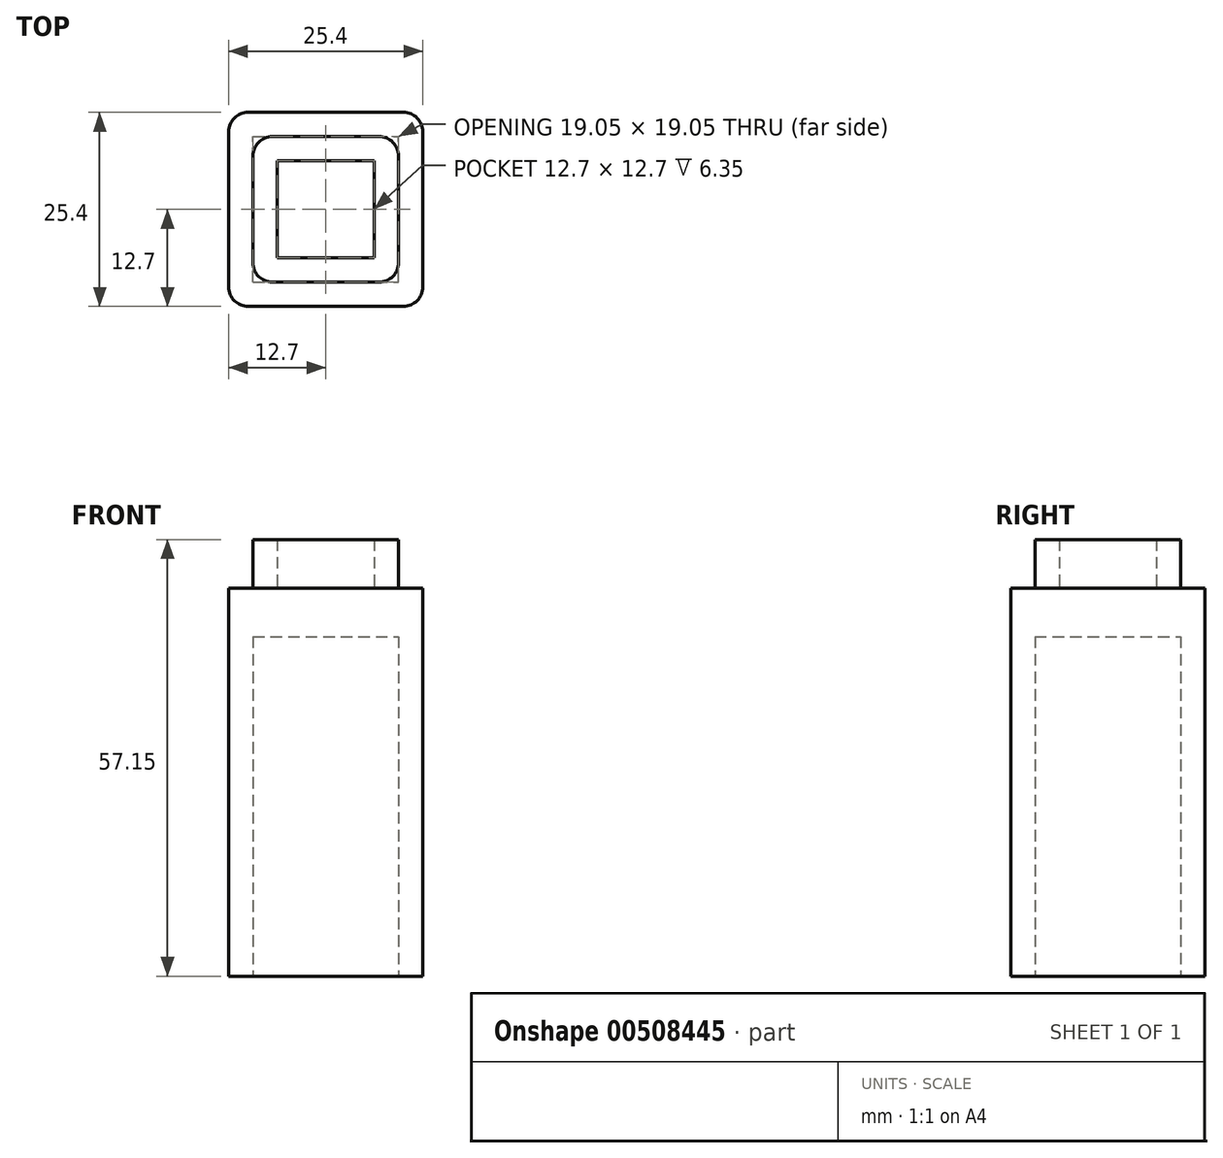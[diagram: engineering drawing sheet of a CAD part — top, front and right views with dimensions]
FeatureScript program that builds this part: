
annotation { "Feature Type Name" : "Feature", "Feature Type Description" : "" }
export const myFeature = defineFeature(function(context is Context, id is Id, definition is map)
    precondition{}
    {
        {
            var Q0;
            Q0=qCreatedBy(makeId("Top.planeOp"),FACE);
            var sketch = newSketch(context, id + "F0", { "sketchPlane" : qUnion([Q0])});
            skLineSegment(sketch, "E0.bottom", {"start": v(0, 0) * mm, "end": v(25.4, 0) * mm});
            skLineSegment(sketch, "E0.top", {"start": v(0, -25.4) * mm, "end": v(25.4, -25.4) * mm});
            skLineSegment(sketch, "E0.left", {"start": v(0, 0) * mm, "end": v(0, -25.4) * mm});
            skLineSegment(sketch, "E0.right", {"start": v(25.4, 0) * mm, "end": v(25.4, -25.4) * mm});
            skSolve(sketch);
        }
        {
            var Q0;
            Q0=qSketchRegion(id+"F0",true);
            var Q1;
            Q1 = qSketchRegion(id + "F2", true);
            extrude(context, id + "F1", {"entities" : qUnion([Q0, Q1]), "depth" : 50.8 * mm});
        }
        {
            var Q0;
            Q0=makeQuery(id+"F1.opExtrude","CAP_FACE",FACE,{"disambiguationData":[OSD([sQuery(id+"F0.wireOp",EDGE,"E0.bottom"),sQuery(id+"F0.wireOp",EDGE,"E0.top"),sQuery(id+"F0.wireOp",EDGE,"E0.left"),sQuery(id+"F0.wireOp",EDGE,"E0.right")])],"isStart":true});
            var sketch = newSketch(context, id + "F2", { "sketchPlane" : qUnion([Q0])});
            skLineSegment(sketch, "E1", {"start": v(0, 0) * mm, "end": v(25.4, 25.4) * mm, "construction": true});
            skLineSegment(sketch, "E2.bottom", {"start": v(3.18, 22.23) * mm, "end": v(22.23, 22.23) * mm});
            skLineSegment(sketch, "E2.top", {"start": v(3.18, 3.18) * mm, "end": v(22.23, 3.18) * mm});
            skLineSegment(sketch, "E2.left", {"start": v(3.18, 22.23) * mm, "end": v(3.18, 3.18) * mm});
            skLineSegment(sketch, "E2.right", {"start": v(22.23, 22.23) * mm, "end": v(22.23, 3.18) * mm});
            skLineSegment(sketch, "E3", {"start": v(3.18, 22.23) * mm, "end": v(22.23, 3.18) * mm, "construction": true});
            skPoint(sketch, "E4", {"position": v(12.7, 12.7) * mm});
            skSolve(sketch);
        }
        {
            var Q0;
            Q0=qSketchRegion(id+"F2",true);
            extrude(context, id + "F3", {"entities" : qUnion([Q0]), "operationType" : NewBodyOperationType.REMOVE, "oppositeDirection" : true, "depth" : 44.45 * mm});
        }
        {
            var Q0;
            Q0=makeQuery(id+"F1.opExtrude","CAP_FACE",FACE,{"disambiguationData":[OSD([sQuery(id+"F0.wireOp",EDGE,"E0.bottom"),sQuery(id+"F0.wireOp",EDGE,"E0.top"),sQuery(id+"F0.wireOp",EDGE,"E0.left"),sQuery(id+"F0.wireOp",EDGE,"E0.right")])],"isStart":false});
            var sketch = newSketch(context, id + "F4", { "sketchPlane" : qUnion([Q0])});
            skLineSegment(sketch, "E5.bottom", {"start": v(6.35, -19.05) * mm, "end": v(19.05, -19.05) * mm});
            skLineSegment(sketch, "E5.top", {"start": v(6.35, -6.35) * mm, "end": v(19.05, -6.35) * mm});
            skLineSegment(sketch, "E5.left", {"start": v(6.35, -19.05) * mm, "end": v(6.35, -6.35) * mm});
            skLineSegment(sketch, "E5.right", {"start": v(19.05, -19.05) * mm, "end": v(19.05, -6.35) * mm});
            skLineSegment(sketch, "E6.bottom", {"start": v(3.18, -22.22) * mm, "end": v(22.23, -22.22) * mm});
            skLineSegment(sketch, "E6.top", {"start": v(3.18, -3.17) * mm, "end": v(22.23, -3.17) * mm});
            skLineSegment(sketch, "E6.left", {"start": v(3.18, -22.22) * mm, "end": v(3.18, -3.17) * mm});
            skLineSegment(sketch, "E6.right", {"start": v(22.23, -22.22) * mm, "end": v(22.23, -3.17) * mm});
            skLineSegment(sketch, "E7", {"start": v(0, 0) * mm, "end": v(25.4, -25.4) * mm, "construction": true});
            skLineSegment(sketch, "E8", {"start": v(6.35, -6.35) * mm, "end": v(19.05, -19.05) * mm, "construction": true});
            skLineSegment(sketch, "E9", {"start": v(3.18, -22.22) * mm, "end": v(22.23, -3.17) * mm, "construction": true});
            skPoint(sketch, "E10", {"position": v(12.7, -12.7) * mm});
            skSolve(sketch);
        }
        {
            var Q0;
            Q0=qSketchRegion(id+"F4",true);
            extrude(context, id + "F5", {"entities" : qUnion([Q0]), "operationType" : NewBodyOperationType.ADD, "depth" : 6.35 * mm});
        }
        {
            var Q0;
            Q0=makeQuery(id+"F1.opExtrude","SWEPT_EDGE",EDGE,{"disambiguationData":[OSD([sQuery(id+"F0.wireOp",EDGE,"E0.bottom"),sQuery(id+"F0.wireOp",EDGE,"E0.left")])]});
            var Q1;
            Q1=makeQuery(id+"F1.opExtrude","SWEPT_EDGE",EDGE,{"disambiguationData":[OSD([sQuery(id+"F0.wireOp",EDGE,"E0.top"),sQuery(id+"F0.wireOp",EDGE,"E0.left")])]});
            var Q2;
            Q2=makeQuery(id+"F1.opExtrude","SWEPT_EDGE",EDGE,{"disambiguationData":[OSD([sQuery(id+"F0.wireOp",EDGE,"E0.bottom"),sQuery(id+"F0.wireOp",EDGE,"E0.right")])]});
            var Q3;
            Q3=makeQuery(id+"F5.opExtrude","SWEPT_EDGE",EDGE,{"disambiguationData":[OSD([sQuery(id+"F4.wireOp",EDGE,"E6.top"),sQuery(id+"F4.wireOp",EDGE,"E6.left")])]});
            var Q4;
            Q4=makeQuery(id+"F5.opExtrude","SWEPT_EDGE",EDGE,{"disambiguationData":[OSD([sQuery(id+"F4.wireOp",EDGE,"E6.bottom"),sQuery(id+"F4.wireOp",EDGE,"E6.left")])]});
            var Q5;
            Q5=makeQuery(id+"F5.opExtrude","SWEPT_EDGE",EDGE,{"disambiguationData":[OSD([sQuery(id+"F4.wireOp",EDGE,"E6.top"),sQuery(id+"F4.wireOp",EDGE,"E6.right")])]});
            var Q6;
            Q6=makeQuery(id+"F5.opExtrude","SWEPT_EDGE",EDGE,{"disambiguationData":[OSD([sQuery(id+"F4.wireOp",EDGE,"E6.bottom"),sQuery(id+"F4.wireOp",EDGE,"E6.right")])]});
            var Q7;
            Q7=makeQuery(id+"F1.opExtrude","SWEPT_EDGE",EDGE,{"disambiguationData":[OSD([sQuery(id+"F0.wireOp",EDGE,"E0.top"),sQuery(id+"F0.wireOp",EDGE,"E0.right")])]});
            fillet(context, id + "F6", {"entities" : qUnion([Q0, Q1, Q2, Q3, Q4, Q5, Q6, Q7]), "radius" : 2.54 * mm, "tangentPropagation" : true, "allowEdgeOverflow" : false});
        }
    });
